# Revit family: Pump_Commercial-Effluent-Zoeller-160_Non-Automatic_Series
name_source: partatom
category: Mechanical Equipment
revit_build: Autodesk Revit 2014 (Build: 20130308_1515(x64)
units: mm (PartAtom-declared; Revit-internal decimal feet)

## types (20) — shared parameters
Cooling = Oil Filled
Cord Length = 240"
Default Elevation = 0"
Description = Sump, Effluent, Dewatering. High Head Flow-Mate 160 Series.
Discharge Diameter = 1 1/2"
Discharge Height = 6"
Discharge Radius = 3/4"
Hardware = Stainless Steel
Height = 19 5/16"
Hertz = 60
Impeller = Bronze
Impeller Type = Non-clogging vortex
Installation Type = Floor Mounted
Insulation = Class B
Lead Wires Insulation = Class B
Length = 10 11/32"
Lower Bearing = Ball bearing
Manufacturer = Zoeller
Material = Cast Iron-Zoeller-Powder Coated Epoxy
Max. Operating Temp. = 130.00 °F
Mechanical Seals = Carbon and Ceramic
Motor Protection = Auto Reset thermal Overload.
Motor Shaft = 416 stainless stee
Motor Type = Submersible
Off Point = 5 1/4"
On Point = 15 3/4"
Operation = Non-Automatic
Price = Prices may vary. Please consult Manufacturer Representative for most up-to-date price list.
Product Documentation Link = http://cdn.qleapahead.com
Product Page URL = http://www.zoellerpumps.com
RPM = 3450
Revised Date = 05/26/2017
Shipping Weight = 80 lbs
Solid Handling = 3/4" Spherical Solids
Square Ring & Gasket = Neoprene
Type Comments = Available in single or double seal designs.
URL = http://www.zoellerpumps.com
Upper Bearing = Ball bearing
Warranty Information = 36 Months (Limited)
Waste Connection = Yes
Width = 8 3/4"

## per-type parameters (varying)
| type | Amps | Apparent Load | Cord Type | Flow @ 5' | Maximum Head | Model | Motor | Phase | Type | Voltage |
| N161-115V/1Ph/15.0A/0.5HP | 15 A | 1725 VA | UL listed, 3-wire neoprene cord and plug (1 Ph) | 100 GPM | 672" | N161 | 1/2 HP | 1 | Permanent Split Capacitor | 115 V |
| E161-230V/1Ph/7.5A/0.5HP | 8 A | 1725 VA | UL listed, 3-wire neoprene cord and plug (1 Ph) | 100 GPM | 672" | E161 | 1/2 HP | 1 | Permanent Split Capacitor | 230 V |
| I161-200V/1Ph/8.8A/0.5HP | 9 A | 1760 VA | UL listed, 3-wire neoprene cord and plug (1 Ph) | 100 GPM | 672" | I161 | 1/2 HP | 1 | Permanent Split Capacitor | 200 V |
| J161-200V/3Ph/6.4A/0.5HP | 6 A | 1280 VA | 4-wire with no plug | 100 GPM | 672" | J161 | 1/2 HP | 3 | 3 Ph | 200 V |
| F161-230V/3Ph/5.2A/0.5HP | 5 A | 1196 VA | 4-wire with no plug | 100 GPM | 672" | F161 | 1/2 HP | 3 | 3 Ph | 230 V |
| G161-460V/3Ph/2.9A/0.5HP | 3 A | 1334 VA | 4-wire with no plug | 100 GPM | 672" | G161 | 1/2 HP | 3 | 3 Ph | 460 V |
| BA161-575V/3Ph/2.4A/0.5HP | 2 A | 1380 VA | 4-wire with no plug | 100 GPM | 672" | BA161 | 1/2 HP | 3 | 3 Ph | 575 V |
| N163-115V/1Ph/15.0A/0.5HP | 15 A | 1725 VA | UL listed 3-wire neoprene cord and plug | 61 GPM | 792" | N163 | 1/2 HP | 1 | Permanent Split Capacitor | 115 V |
| E163-230V/1Ph/7.5A/0.5HP | 8 A | 1725 VA | UL listed 3-wire neoprene cord and plug | 63 GPM | 792" | E163 | 1/2 HP | 1 | Permanent Split Capacitor | 230 V |
| I163-200V/1Ph/8.5A/0.5HP | 9 A | 1700 VA | UL listed 3-wire neoprene cord and plug | 63 GPM | 792" | I163 | 1/2 HP | 1 | Permanent Split Capacitor | 200 V |
| J163-200V/3Ph/6.0A/0.5HP | 6 A | 1200 VA | 4-wire with no plug | 63 GPM | 792" | J163 | 1/2 HP | 3 | 3 Ph | 200 V |
| F163-230V/3Ph/4.8A/0.5HP | 5 A | 1104 VA | 4-wire with no plug | 63 GPM | 792" | F163 | 1/2 HP | 3 | 3 Ph | 230 V |
| G163-460V/3Ph/2.9A/0.5HP | 3 A | 1334 VA | 4-wire with no plug | 63 GPM | 792" | G163 | 1/2 HP | 3 | 3 Ph | 460 V |
| BA163-575V/3Ph/2.4A/0.5HP | 2 A | 1380 VA | 4-wire with no plug | 63 GPM | 792" | BA163 | 1/2 HP | 3 | 3 Ph | 575 V |
| E165-230V/1Ph/10.2A/1.0HP | 10 A | 2346 VA | UL listed 3-wire neoprene cord and plug | 61 GPM | 1038" | E165 | 1.0 HP | 1 | Permanent Split Capacitor | 230 V |
| I165-200V/1Ph/12.6A/1.0HP | 13 A | 2520 VA | UL listed 3-wire neoprene cord and plug | 61 GPM | 1038" | I165 | 1.0 HP | 1 | Permanent Split Capacitor | 200 V |
| J165-200V/3Ph/7.5A/1.0HP | 8 A | 1500 VA | 4-wire with no plug | 61 GPM | 1038" | J165 | 1.0 HP | 3 | 3 Ph | 200 V |
| F165-230V/3Ph/7.4A/1.0HP | 7 A | 1702 VA | 4-wire with no plug | 61 GPM | 1038" | F165 | 1.0 HP | 3 | 3 Ph | 230 V |
| G165-460V/3Ph/3.7A/1.0HP | 4 A | 1702 VA | 4-wire with no plug | 61 GPM | 1038" | G165 | 1.0 HP | 3 | 3 Ph | 460 V |
| BA165-575V/3Ph/3.0A/1.0HP | 3 A | 1725 VA | 4-wire with no plug | 61 GPM | 1038" | BA165 | 1.0 HP | 3 | 3 Ph | 575 V |

## geometry (parser evidence)
native form markers: Blend x4, Sweep x3
no freeform markers — native parametric forms only
